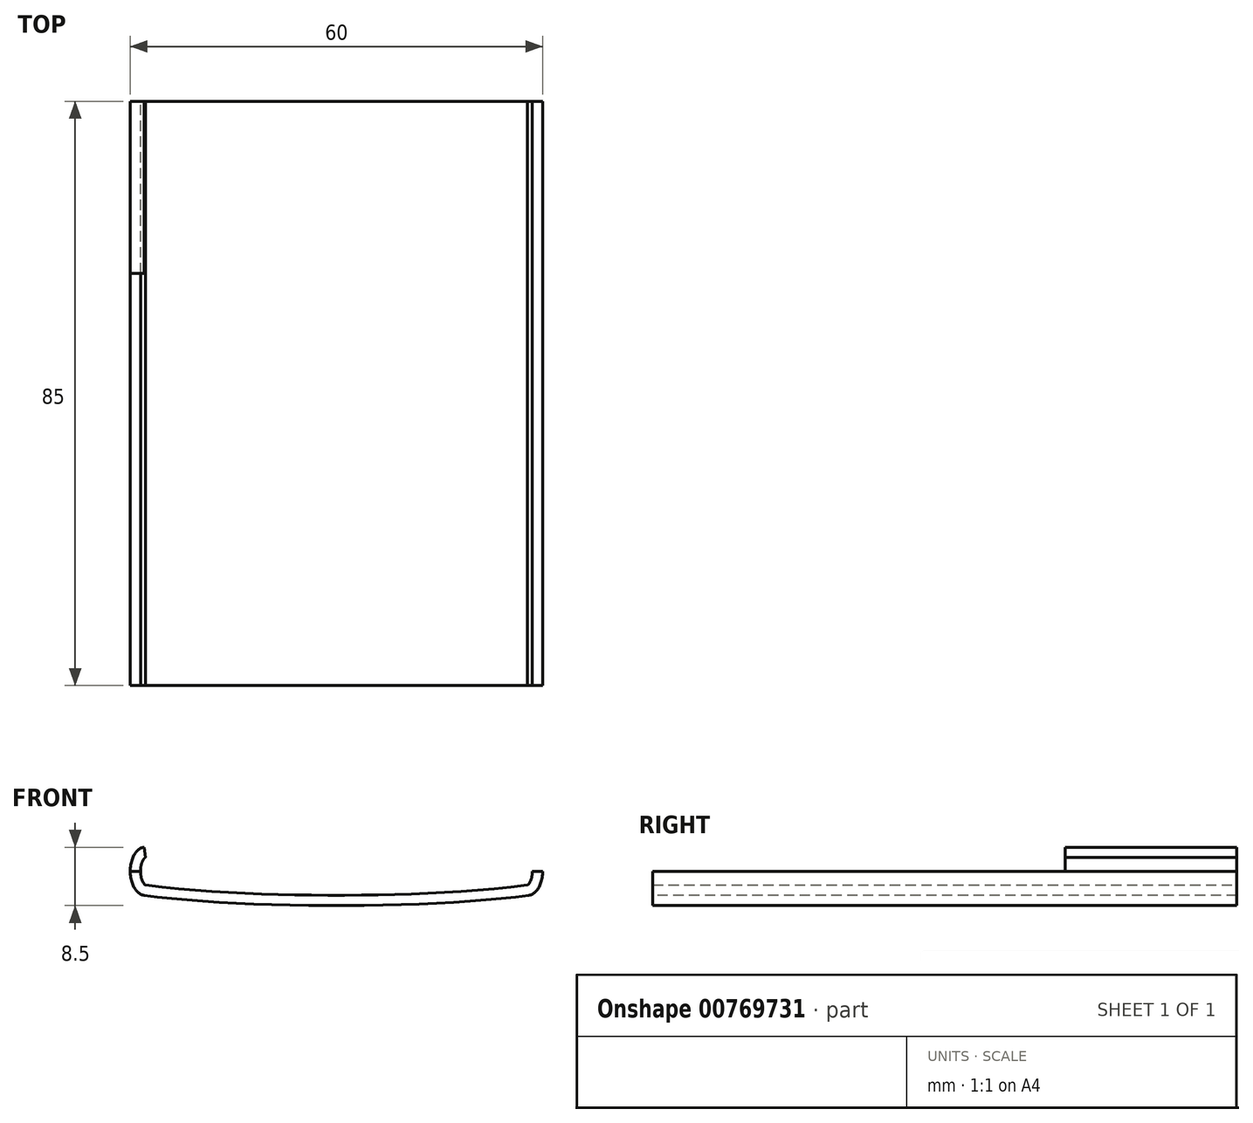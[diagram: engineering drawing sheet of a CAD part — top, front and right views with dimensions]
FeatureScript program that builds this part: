
annotation { "Feature Type Name" : "Feature", "Feature Type Description" : "" }
export const myFeature = defineFeature(function(context is Context, id is Id, definition is map)
    precondition{}
    {
        {
            var Q0;
            Q0=qCreatedBy(makeId("Front.planeOp"),FACE);
            var sketch = newSketch(context, id + "F0", { "sketchPlane" : qUnion([Q0])});
            skEllipse(sketch, "E0", {"center": v(0, 0) * mm, "majorRadius": 39.2 * mm, "minorRadius": 5 * mm, "majorAxis": v(1, 0)});
            skLineSegment(sketch, "E1", {"start": v(0, 5) * mm, "end": v(0, -5) * mm});
            skLineSegment(sketch, "E2", {"start": v(-39.2, 0) * mm, "end": v(39.2, 0) * mm, "construction": true});
            skLineSegment(sketch, "E3", {"start": v(-28, 3.5) * mm, "end": v(-28, -3.5) * mm, "construction": true});
            skEllipse(sketch, "E4", {"center": v(-27.83, 0) * mm, "majorRadius": 2.17 * mm, "minorRadius": 3.51 * mm, "majorAxis": v(1, 0)});
            skPoint(sketch, "E5", {"position": v(-30, 0) * mm});
            skSolve(sketch);
        }
        {
            var Q0;
            {var subQ0=sQuery(id+"F0.wireOp",EDGE,"E4");var subQ1=sQuery(id+"F0.wireOp",EDGE,"E0");var subQ2=makeQuery(id+"F0.imprint","INTERSECT",VERTEX,{"disambiguationData":[OD(0.0)],"derivedFrom":[subQ1,subQ0]});Q0=makeQuery(id+"F0.imprint","IMPRINT",FACE,{"disambiguationData":[TD([[makeQuery(id+"F0.imprint","IMPRINT",EDGE,{"disambiguationData":[TD([[subQ2,1.0]])],"derivedFrom":subQ0}),1.0]])]});}
            var Q1;
            {var subQ0=sQuery(id+"F0.wireOp",EDGE,"E1");Q1=makeQuery(id+"F0.imprint","IMPRINT",FACE,{"disambiguationData":[TD([[makeQuery(id+"F0.imprint","IMPRINT",EDGE,{"derivedFrom":subQ0}),-1.0]])]});}
            extrude(context, id + "F1", {"entities" : qUnion([Q0, Q1]), "depth" : 85 * mm, "offsetDistance" : 25 * mm});
        }
        {
            var Q0;
            Q0=makeQuery(id+"F1.opExtrude","SWEPT_BODY",BODY,{"disambiguationData":[OSD([sQuery(id+"F0.wireOp",EDGE,"E0"),sQuery(id+"F0.wireOp",EDGE,"E1"),sQuery(id+"F0.wireOp",EDGE,"E4")])]});
            var Q1;
            Q1=makeQuery(id+"F1.opExtrude","SWEPT_FACE",FACE,{"disambiguationData":[OSD([sQuery(id+"F0.wireOp",EDGE,"E1")])]});
            mirror(context, id + "F2", {"operationType" : NewBodyOperationType.ADD, "entities" : qUnion([Q0]), "mirrorPlane" : qUnion([Q1])});
        }
        {
            var Q0;
            {var subQ0=makeQuery(id+"F1.opExtrude","CAP_FACE",FACE,{"disambiguationData":[OSD([sQuery(id+"F0.wireOp",EDGE,"E0"),sQuery(id+"F0.wireOp",EDGE,"E1"),sQuery(id+"F0.wireOp",EDGE,"E4")])],"isStart":false});Q0=makeQuery(id+"F2.boolean.opBoolean","MERGE",FACE,{"derivedFrom":[subQ0,makeQuery(id+"F2.opPattern","COPY",FACE,{"derivedFrom":subQ0,"instanceName":"1"})]});}
            var Q1;
            {var subQ0=makeQuery(id+"F1.opExtrude","CAP_FACE",FACE,{"disambiguationData":[OSD([sQuery(id+"F0.wireOp",EDGE,"E0"),sQuery(id+"F0.wireOp",EDGE,"E1"),sQuery(id+"F0.wireOp",EDGE,"E4")])],"isStart":true});Q1=makeQuery(id+"F2.boolean.opBoolean","MERGE",FACE,{"derivedFrom":[subQ0,makeQuery(id+"F2.opPattern","COPY",FACE,{"derivedFrom":subQ0,"instanceName":"1"})]});}
            shell(context, id + "F3", {"entities" : qUnion([Q0, Q1]), "thickness" : 1.5 * mm});
        }
        {
            var Q0;
            Q0=qCreatedBy(makeId("Front.planeOp"),FACE);
            var sketch = newSketch(context, id + "F4", { "sketchPlane" : qUnion([Q0])});
            skLineSegment(sketch, "E6.bottom", {"start": v(-30.82, 0) * mm, "end": v(30.82, 0) * mm});
            skLineSegment(sketch, "E6.top", {"start": v(-30.82, 8.72) * mm, "end": v(30.82, 8.72) * mm});
            skLineSegment(sketch, "E6.left", {"start": v(-30.82, 0) * mm, "end": v(-30.82, 8.72) * mm});
            skLineSegment(sketch, "E6.right", {"start": v(30.82, 0) * mm, "end": v(30.82, 8.72) * mm});
            skSolve(sketch);
        }
        {
            var Q0;
            Q0 = qSketchRegion(id + "F4", true);
            extrude(context, id + "F5", {"entities" : qUnion([Q0]), "operationType" : NewBodyOperationType.REMOVE, "endBound" : BoundingType.THROUGH_ALL, "depth" : 25 * mm, "offsetDistance" : 25 * mm});
        }
        {
            var Q0;
            Q0=qCreatedBy(makeId("Front.planeOp"),FACE);
            var sketch = newSketch(context, id + "F6", { "sketchPlane" : qUnion([Q0])});
            skFitSpline(sketch, "E7.0", {"points": [v(-28.5, 0) * mm, v(-28.5, -0.18) * mm, v(-28.48, -0.46) * mm, v(-28.42, -0.82) * mm, v(-28.35, -1.09) * mm, v(-28.26, -1.35) * mm, v(-28.17, -1.56) * mm, v(-28.08, -1.72) * mm, v(-28, -1.83) * mm, v(-27.92, -1.92) * mm, v(-27.85, -1.98) * mm, v(-27.82, -2) * mm, v(-27.8, -2.01) * mm]});
            skEllipticalArc(sketch, "E8.0", {});
            skEllipticalArc(sketch, "E9.MirrorCS", {});
            skFitSpline(sketch, "E10.MirrorCS", {"points": [v(-28.5, 0) * mm, v(-28.5, 0.18) * mm, v(-28.48, 0.46) * mm, v(-28.42, 0.82) * mm, v(-28.35, 1.09) * mm, v(-28.26, 1.35) * mm, v(-28.17, 1.56) * mm, v(-28.08, 1.72) * mm, v(-28, 1.83) * mm, v(-27.92, 1.92) * mm, v(-27.85, 1.98) * mm, v(-27.82, 2) * mm, v(-27.8, 2.01) * mm]});
            skLineSegment(sketch, "E11", {"start": v(-28, 3.5) * mm, "end": v(-27.8, 2.01) * mm});
            skLineSegment(sketch, "E12", {"start": v(-27.8, -2.01) * mm, "end": v(-28, -3.5) * mm});
            skLineSegment(sketch, "E13", {"start": v(-27, 0) * mm, "end": v(-29.4, 2.4) * mm});
            const initialGuessF6  = {"E8.0": [-0.027825342465753425, 0, 0, 1, 0.0035113432694302326, 0.002174657534246576, 1.5707963267948966, 3.0611910961766875], "E9.MirrorCS": [-0.027825342465753425, 0, 0, -1, 0.0035113432694302326, 0.002174657534246576, 3.2219942110028987, 4.71238898038469]};
            skSetInitialGuess(sketch, initialGuessF6);
            skSolve(sketch);
        }
        {
            var Q0;
            Q0 = qSketchRegion(id + "F6", true);
            extrude(context, id + "F7", {"entities" : qUnion([Q0]), "operationType" : NewBodyOperationType.ADD, "depth" : 25 * mm, "offsetDistance" : 25 * mm});
        }
    });
